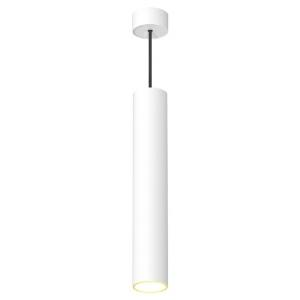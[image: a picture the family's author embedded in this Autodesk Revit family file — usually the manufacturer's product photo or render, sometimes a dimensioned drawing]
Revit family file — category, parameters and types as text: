
# Revit family: hangover_810-0550-H30-K20
name_source: partatom
category: Leuchten
revit_build: Autodesk Revit 2018 (Build: 20190510_1515(x64)
units: mm (PartAtom-declared; Revit-internal decimal feet)

## family parameters
Basisbauteil = Fläche
Beim Laden mit Abzugskörper schneiden = Nein
Bemaßung runder Anschluss = Durchmesser verwenden
Gemeinsam genutzt = Nein
Lichtquelle = Nein
Raumberechnungspunkt = Nein
Teiletyp = Normal

## types (1)
- 810-0550-H30-K20-L00
    Beschreibung = HANGOVER
    CIE Flux Codes = 90 96 99 100 85
    Color Rendering = 1A/90…99
    Color Temperature = 2700K
    Height = 450 mm
    Hersteller = Prolicht
    Lamp Light Flux = 1782 lm
    Lamp Power = 20 W
    Lamp count = 1
    Lampe = 1 x LED
    Length = 75 mm
    Luminous efficacy = 76 lm/W
    ModVariant = Nein
    Modell = 810-0550
    Mounting Place = Ceiling
    Mounting Type = Pendant
    Number of Poles = 1
    OnlyDefault = Ja
    Power Factor = 1
    Product Name = HANGOVER
    Product group = Suspended spotlights
    ProductGroupID = 942
    Protection Class = Protection class
    Protection Degree = Degree of protection
    RLX_Detail_Level = 1
    Scheinlast = 20 VA
    Socket = socket
    Standby Power = 0 W
    System Light Flux = 1512 lm
    System Power = 10 W
    Typenbild = 410-7590.jpg
    Typenkommentare = LED COLOUR DIR 2700 K (27),REFLECTOR 20° (20),SHINE RING ABSICHTLICH_LEER (00)
    URL = http://prolicht.at
    VarID = 810-0550-h30-k20-l00
    Voltage = 0 V
    Vorgabe-Ansicht = 1800 mm
    Weight = 0.00 kg
    Width = 0 mm  [stored 0 ft]

note: [stored X ft] marks values corroborated as IEEE doubles in the binary element streams (Revit-internal decimal feet)

## geometry (parser evidence)
native form markers: Sweep x7
no freeform markers — native parametric forms only
